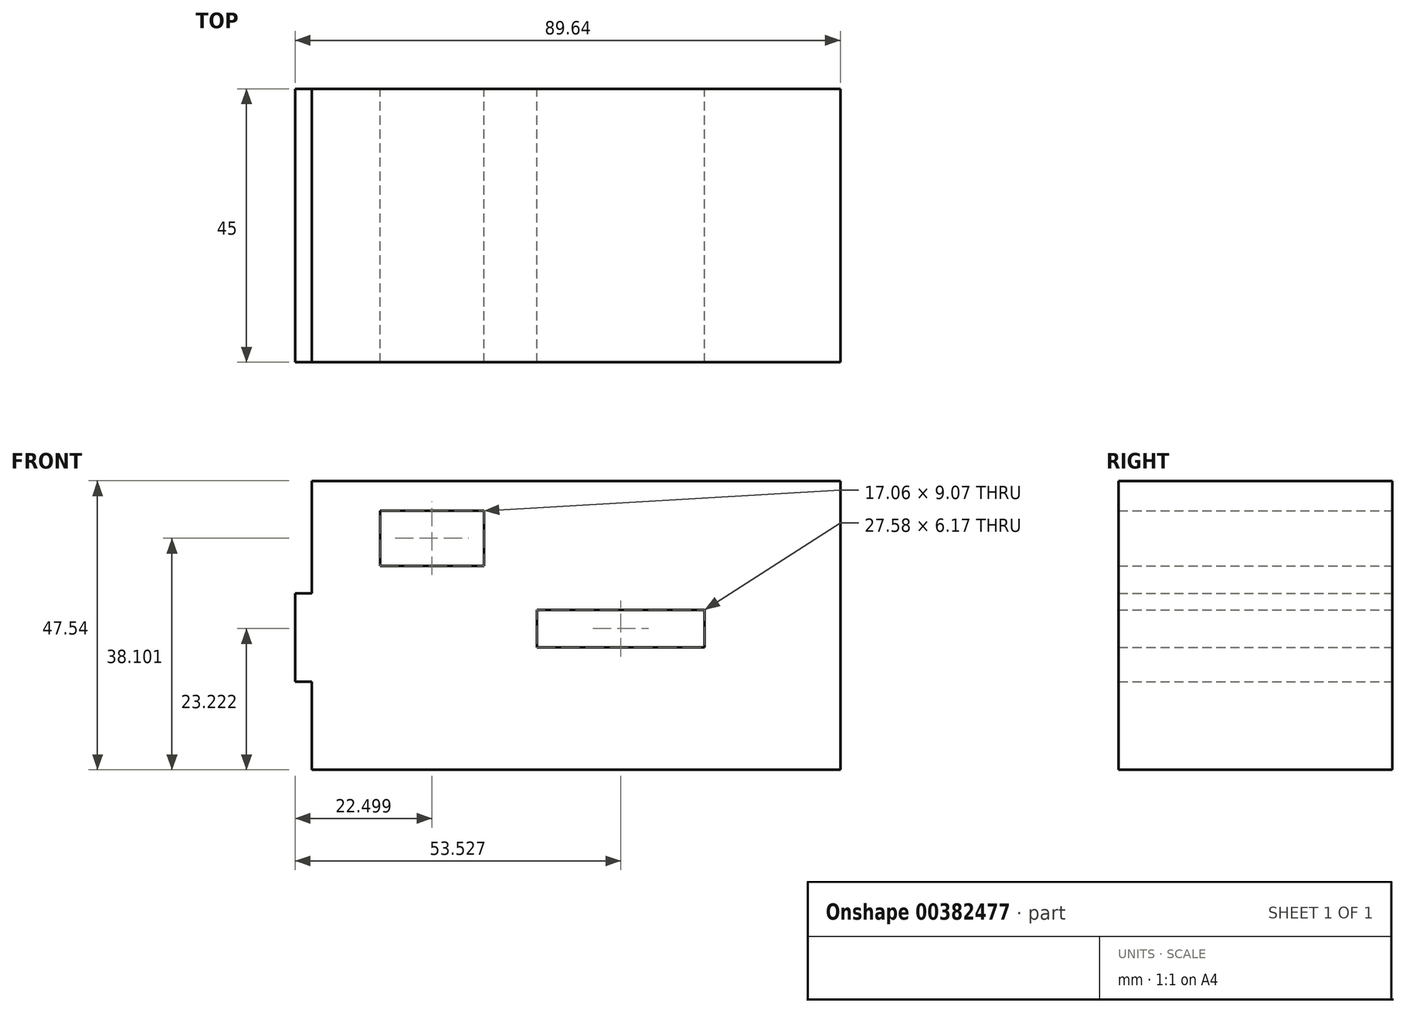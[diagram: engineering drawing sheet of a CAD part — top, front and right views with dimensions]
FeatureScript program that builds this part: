
annotation { "Feature Type Name" : "Feature", "Feature Type Description" : "" }
export const myFeature = defineFeature(function(context is Context, id is Id, definition is map)
    precondition{}
    {
        {
            var Q0;
            Q0=qCreatedBy(makeId("Front.planeOp"),FACE);
            var sketch = newSketch(context, id + "F0", { "sketchPlane" : qUnion([Q0])});
            skLineSegment(sketch, "E0.bottom", {"start": v(-37.38, 18.33) * mm, "end": v(49.54, 18.33) * mm});
            skLineSegment(sketch, "E0.top", {"start": v(-37.38, -29.21) * mm, "end": v(49.54, -29.21) * mm});
            skLineSegment(sketch, "E0.left", {"start": v(-37.38, 18.33) * mm, "end": v(-37.38, -29.21) * mm});
            skLineSegment(sketch, "E0.right", {"start": v(49.54, 18.33) * mm, "end": v(49.54, -29.21) * mm});
            skLineSegment(sketch, "E1.bottom", {"start": v(-9.07, 4.35) * mm, "end": v(-26.13, 4.35) * mm});
            skLineSegment(sketch, "E1.top", {"start": v(-9.07, 13.43) * mm, "end": v(-26.13, 13.43) * mm});
            skLineSegment(sketch, "E1.left", {"start": v(-9.07, 4.35) * mm, "end": v(-9.07, 13.43) * mm});
            skLineSegment(sketch, "E1.right", {"start": v(-26.13, 4.35) * mm, "end": v(-26.13, 13.43) * mm});
            skPoint(sketch, "E1.middle", {"position": v(-17.6, 8.9) * mm});
            skLineSegment(sketch, "E2.bottom", {"start": v(27.22, -9.07) * mm, "end": v(-0.36, -9.07) * mm});
            skLineSegment(sketch, "E2.top", {"start": v(27.22, -2.9) * mm, "end": v(-0.36, -2.9) * mm});
            skLineSegment(sketch, "E2.left", {"start": v(27.22, -9.07) * mm, "end": v(27.22, -2.9) * mm});
            skLineSegment(sketch, "E2.right", {"start": v(-0.36, -9.07) * mm, "end": v(-0.36, -2.9) * mm});
            skPoint(sketch, "E2.middle", {"position": v(13.43, -5.99) * mm});
            skLineSegment(sketch, "E3.bottom", {"start": v(-18.69, -14.7) * mm, "end": v(-40.1, -14.7) * mm});
            skLineSegment(sketch, "E3.top", {"start": v(-18.69, -0.18) * mm, "end": v(-40.1, -0.18) * mm});
            skLineSegment(sketch, "E3.left", {"start": v(-18.69, -14.7) * mm, "end": v(-18.69, -0.18) * mm});
            skLineSegment(sketch, "E3.right", {"start": v(-40.1, -14.7) * mm, "end": v(-40.1, -0.18) * mm});
            skPoint(sketch, "E3.middle", {"position": v(-29.4, -7.44) * mm});
            skSolve(sketch);
        }
        {
            var Q0;
            Q0 = qSketchRegion(id + "F0", true);
            extrude(context, id + "F1", {"entities" : qUnion([Q0]), "depth" : 45 * mm});
        }
    });
